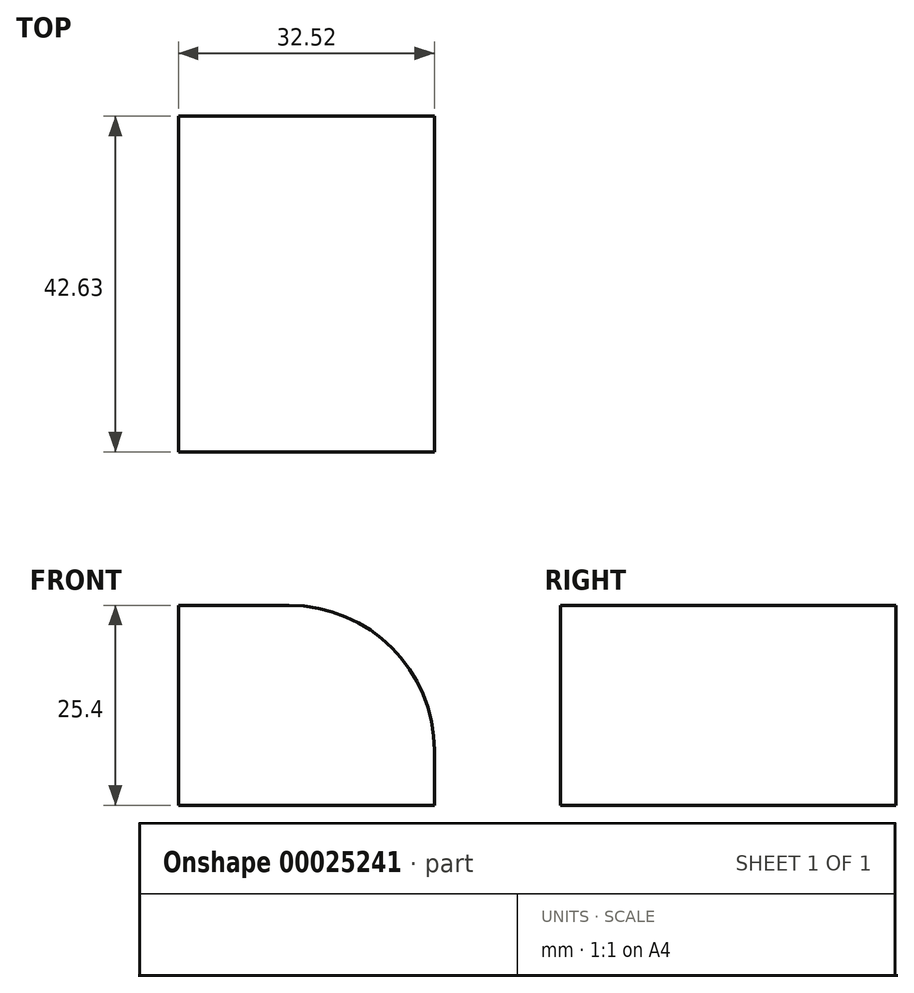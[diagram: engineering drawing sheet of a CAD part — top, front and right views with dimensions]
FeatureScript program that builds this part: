
annotation { "Feature Type Name" : "Feature", "Feature Type Description" : "" }
export const myFeature = defineFeature(function(context is Context, id is Id, definition is map)
    precondition{}
    {
        {
            var Q0;
            Q0=qCreatedBy(makeId("Top.planeOp"),FACE);
            var sketch = newSketch(context, id + "F0", { "sketchPlane" : qUnion([Q0])});
            skLineSegment(sketch, "E0.bottom", {"start": v(0, 0) * mm, "end": v(-32.52, 0) * mm});
            skLineSegment(sketch, "E0.top", {"start": v(0, 42.63) * mm, "end": v(-32.52, 42.63) * mm});
            skLineSegment(sketch, "E0.left", {"start": v(0, 0) * mm, "end": v(0, 42.63) * mm});
            skLineSegment(sketch, "E0.right", {"start": v(-32.52, 0) * mm, "end": v(-32.52, 42.63) * mm});
            skSolve(sketch);
        }
        {
            var Q0;
            Q0=makeQuery(id+"F0.imprint","IMPRINT",FACE,{"disambiguationData":[TD([[makeQuery(id+"F0.imprint","IMPRINT",EDGE,{"derivedFrom":sQuery(id+"F0.wireOp",EDGE,"E0.bottom")}),-1.0]])]});
            extrude(context, id + "F1", {"entities" : qUnion([Q0]), "oppositeDirection" : true, "depth" : 25.4 * mm});
        }
        {
            var Q0;
            Q0=makeQuery(id+"F1.opExtrude","CAP_EDGE",EDGE,{"disambiguationData":[OSD([sQuery(id+"F0.wireOp",EDGE,"E0.left")])],"isStart":true});
            fillet(context, id + "F2", {"entities" : qUnion([Q0]), "radius" : 18.45 * mm, "tangentPropagation" : true, "allowEdgeOverflow" : false});
        }
    });
